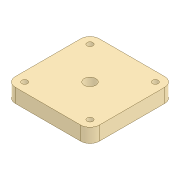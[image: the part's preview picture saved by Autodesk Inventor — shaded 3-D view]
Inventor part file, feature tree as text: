
AUTODESK INVENTOR PART (.ipt)
format: ipt  version: 2020 (Build 240168000, 168)  size: 113,664 bytes
history: native  units: mm
features: mirror x2, other x1, extrude x1, sketch x1
ambient origin geometry x8: Origin, YZ Plane, XZ Plane, XY Plane, X Axis, Y Axis, Z Axis, Center Point
bodies: Body1 (feature_tree)
feature tree (5):
  other  "Sólido1"
  extrude  "Extrusão1"  Depth=36.0mm
  mirror  "Espelhamento1"
  mirror  "Espelhamento2"
  sketch  "Esboço1"  dims[d0=10.0mm d1=36.0mm d2=36.0mm d3=8.0mm d4=5.0mm d5=12.0mm d6=0.0mm d7=8.0mm d8=8.0mm]
